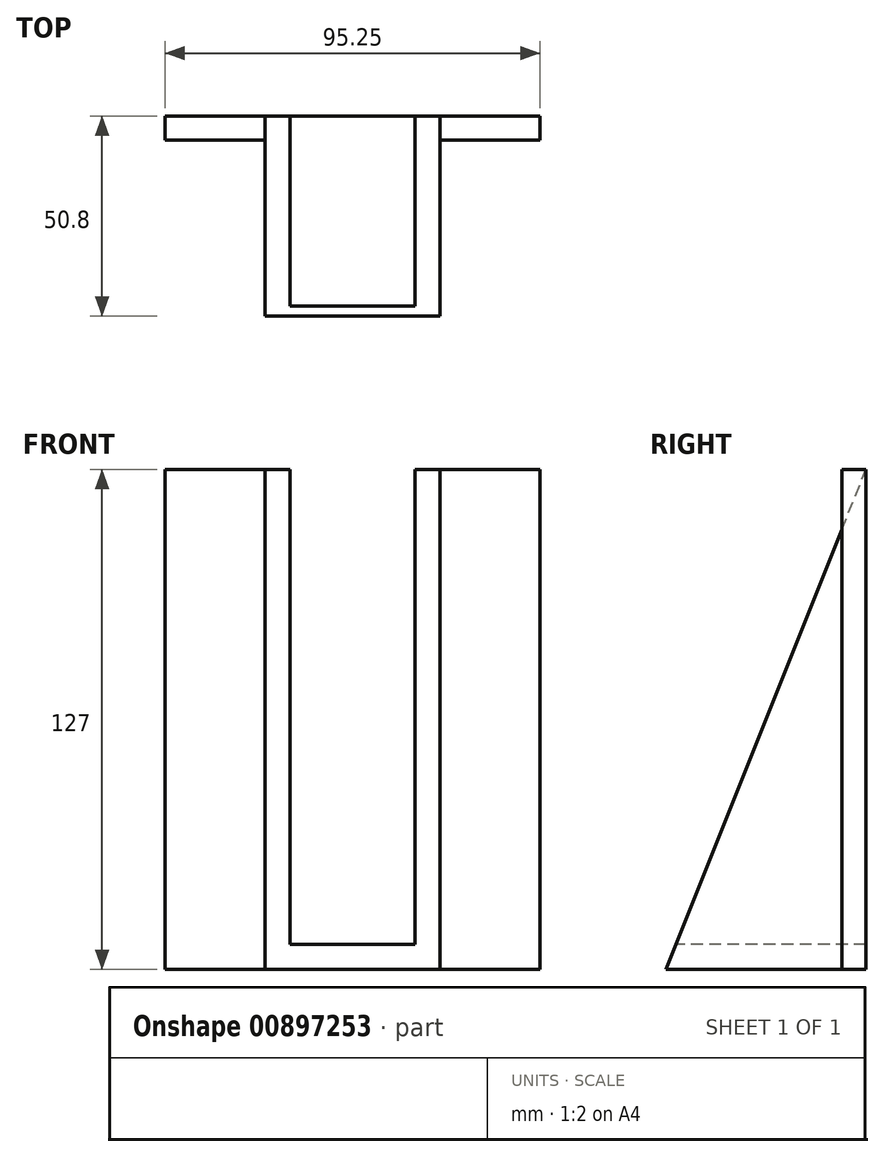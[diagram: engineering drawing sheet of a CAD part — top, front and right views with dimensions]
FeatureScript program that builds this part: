
annotation { "Feature Type Name" : "Feature", "Feature Type Description" : "" }
export const myFeature = defineFeature(function(context is Context, id is Id, definition is map)
    precondition{}
    {
        {
            var Q0;
            Q0=qCreatedBy(makeId("Right.planeOp"),FACE);
            var sketch = newSketch(context, id + "F0", { "sketchPlane" : qUnion([Q0])});
            skLineSegment(sketch, "E0", {"start": v(0, 0) * mm, "end": v(50.8, 127) * mm});
            skLineSegment(sketch, "E1", {"start": v(50.8, 127) * mm, "end": v(50.8, 0) * mm});
            skLineSegment(sketch, "E2", {"start": v(50.8, 0) * mm, "end": v(0, 0) * mm});
            skSolve(sketch);
        }
        {
            var Q0;
            Q0=makeQuery(id+"F0.imprint","IMPRINT",FACE,{"disambiguationData":[TD([[makeQuery(id+"F0.imprint","IMPRINT",EDGE,{"derivedFrom":sQuery(id+"F0.wireOp",EDGE,"E0")}),-1.0]])]});
            extrude(context, id + "F1", {"entities" : qUnion([Q0]), "depth" : 44.45 * mm, "offsetDistance" : 25.4 * mm});
        }
        {
            var Q0;
            Q0=makeQuery(id+"F1.opExtrude","SWEPT_FACE",FACE,{"disambiguationData":[OSD([sQuery(id+"F0.wireOp",EDGE,"E1")])]});
            var sketch = newSketch(context, id + "F2", { "sketchPlane" : qUnion([Q0])});
            skLineSegment(sketch, "E3.bottom", {"start": v(-44.45, 127) * mm, "end": v(-69.85, 127) * mm});
            skLineSegment(sketch, "E3.top", {"start": v(-44.45, 0) * mm, "end": v(-69.85, 0) * mm});
            skLineSegment(sketch, "E3.left", {"start": v(-44.45, 127) * mm, "end": v(-44.45, 0) * mm});
            skLineSegment(sketch, "E3.right", {"start": v(-69.85, 127) * mm, "end": v(-69.85, 0) * mm});
            skLineSegment(sketch, "E4.bottom", {"start": v(0, 127) * mm, "end": v(25.4, 127) * mm});
            skLineSegment(sketch, "E4.top", {"start": v(0, 0) * mm, "end": v(25.4, 0) * mm});
            skLineSegment(sketch, "E4.left", {"start": v(0, 127) * mm, "end": v(0, 0) * mm});
            skLineSegment(sketch, "E4.right", {"start": v(25.4, 127) * mm, "end": v(25.4, 0) * mm});
            skSolve(sketch);
        }
        {
            var Q0;
            Q0=makeQuery(id+"F2.imprint","IMPRINT",FACE,{"disambiguationData":[TD([[makeQuery(id+"F2.imprint","IMPRINT",EDGE,{"derivedFrom":sQuery(id+"F2.wireOp",EDGE,"E4.bottom")}),-1.0]])]});
            var Q1;
            Q1=makeQuery(id+"F2.imprint","IMPRINT",FACE,{"disambiguationData":[TD([[makeQuery(id+"F2.imprint","IMPRINT",EDGE,{"derivedFrom":sQuery(id+"F2.wireOp",EDGE,"E3.bottom")}),1.0]])]});
            extrude(context, id + "F3", {"entities" : qUnion([Q0, Q1]), "operationType" : NewBodyOperationType.ADD, "oppositeDirection" : true, "depth" : 6.1 * mm, "offsetDistance" : 25.4 * mm});
        }
        {
            var Q0;
            Q0=makeQuery(id+"F1.opExtrude","SWEPT_FACE",FACE,{"disambiguationData":[OSD([sQuery(id+"F0.wireOp",EDGE,"E0")])]});
            var Q1;
            Q1=makeQuery(id+"F3.boolean.opBoolean","MERGE",FACE,{"derivedFrom":[makeQuery(id+"F1.opExtrude","SWEPT_FACE",FACE,{"disambiguationData":[OSD([sQuery(id+"F0.wireOp",EDGE,"E1")])]}),makeQuery(id+"F3.opExtrude","CAP_FACE",FACE,{"disambiguationData":[OSD([sQuery(id+"F2.wireOp",EDGE,"E3.bottom"),sQuery(id+"F2.wireOp",EDGE,"E3.top"),sQuery(id+"F2.wireOp",EDGE,"E3.left"),sQuery(id+"F2.wireOp",EDGE,"E3.right")])],"isStart":true}),makeQuery(id+"F3.opExtrude","CAP_FACE",FACE,{"disambiguationData":[OSD([sQuery(id+"F2.wireOp",EDGE,"E4.bottom"),sQuery(id+"F2.wireOp",EDGE,"E4.top"),sQuery(id+"F2.wireOp",EDGE,"E4.left"),sQuery(id+"F2.wireOp",EDGE,"E4.right")])],"isStart":true})]});
            shell(context, id + "F4", {"entities" : qUnion([Q0, Q1]), "thickness" : 6.35 * mm});
        }
    });
